# Revit family: Sunshade-Linear-Kawneer-Curtain_Wall-Curved
name_source: partatom
category: Specialty Equipment
revit_build: Autodesk Revit 2015 (Build: 20140905_0730(x64)
units: mm (PartAtom-declared; Revit-internal decimal feet)

## types (1)
- 30"-Circular
    Blade Count = 5
    Blade Type = Blade-Kawneer-Circular : Versoleil
    Blades Distance = 0' - 4 1/2"
    Bottom Inset Distance = 0' - 5"
    CTRL Length = 2' - 6"
    Default Elevation = 4' - 0"
    Description = Square Outrigger, Rectangle Fascias
    Distance Blade 1 and 2 = 0' - 0 1/8"
    Distance Blade 2 and 3 = 0' - 0 7/16"
    Distance Blade 3 and 4 = 0' - 0 11/16"
    Distance Blade 4 and 5 = 0' - 0 15/16"
    Distance Blade 5 and 6 = 0' - 0 7/8"
    Finish = Aluminum - Kawneer - Clear
    Has 6th Blade = No
    Length = 2' - 6"
    Manufacturer = Kawneer
    Model = Sunshade Linear
    Product Documentation Link = http://www.kawneer.com
    Product Page URL = http://www.kawneer.com
    Product data url = https://bimobject.com
    URL = http://www.kawneer.com

## geometry (parser evidence)
native form markers: Sweep x9
no freeform markers — native parametric forms only
